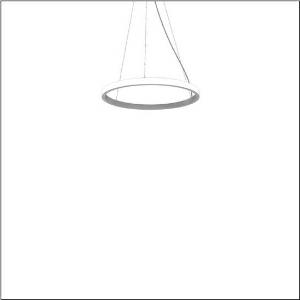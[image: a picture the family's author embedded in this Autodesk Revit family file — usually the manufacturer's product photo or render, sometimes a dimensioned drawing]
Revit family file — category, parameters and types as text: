
# Revit family: silica_21_ring-o_5pjbo1d3204a
name_source: partatom
category: Lighting Fixtures
units: mm (PartAtom-declared; Revit-internal decimal feet)

## family parameters
Cut with Voids When Loaded = No
Host = Face
Light Source = No
Part Type = Normal
Room Calculation Point = No
Round Connector Dimension = Use Diameter
Shared = No

## types (1)
- Silica 21 Ring-O (1 x LED, 3930 lm, 60 W, 4000K)
    Apparent Load = 60 VA
    CIE Flux Codes = 2 16 49 50 100
    Color Rendering = 80
    Color Temperature = 4000K
    Default Elevation = 1800 mm
    Description = Silica 21 Ring-O, suspended luminaire, of PMMA, frosted, light emission: outer ring side luminous distribution, primary light characteristic: symmetric, installation type: suspended mounting, LED, rated luminous flux: 3.930lm, luminous efficacy: 66lm/W, light colour: 840, colour temperature: 4000K, control gear: DALI 2, with terminal, 5-pole, mains connection: 230V, AC/DC, 0/50..60Hz, rated input power: 60W, housing, of extruded aluminium section, metallic grey (RAL 9006), diameter: 610mm, ceiling canopy, metallic grey (RAL 9006), protection rating (lamp compartment): IP40, insulation class (complete): insulation class I (protective earthing), certification: CE, impact resistance: IK02, permissible operating ambient temperature: 0..+35°C, packaging unit: 1 piece
    Height = 48 mm  [stored 0.15748 ft]
    Lamp = 1 x LED
    Lamp Light Flux = 3930 lm
    Lamp Power = 60 W
    Lamp count = 1
    Length = 610 mm
    Luminous efficacy = 66 lm/W
    Manufacturer = Siteco
    ModVariant = No
    Model = 5PJBO1D3204A
    Mounting Place = Ceiling
    Mounting Type = Pendant
    Number of Poles = 1
    OnlyDefault = Yes
    Power Factor = 1
    Product Name = Silica 21 Ring-O
    Product group = suspended luminaire
    ProductGroupID = 904
    Protection Class = Protection class I
    Protection Degree = IP 40
    RLX_Detail_Level = 1
    RLX_Emergency_Light_Flux = 0 lm
    RLX_Emergency_Type = 0
    RLX_Emergency_Type_DB = No
    RlxData = <blob elided: 11621 chars, md5=695d5dd9>
    Socket = socket
    Standby Power = 0 W
    System Light Flux = 3930 lm
    System Power = 60 W
    Type Comments = Product without accessories
    Type Image = l_1251758.jpg
    URL = http://relux.com
    VarID = ---
    Voltage = 0 V
    Weight = 0.00 kg
    Width = 0 mm  [stored 0 ft]

note: [stored X ft] marks values corroborated as IEEE doubles in the binary element streams (Revit-internal decimal feet)

## geometry (parser evidence)
native form markers: Sweep x12
no freeform markers — native parametric forms only
